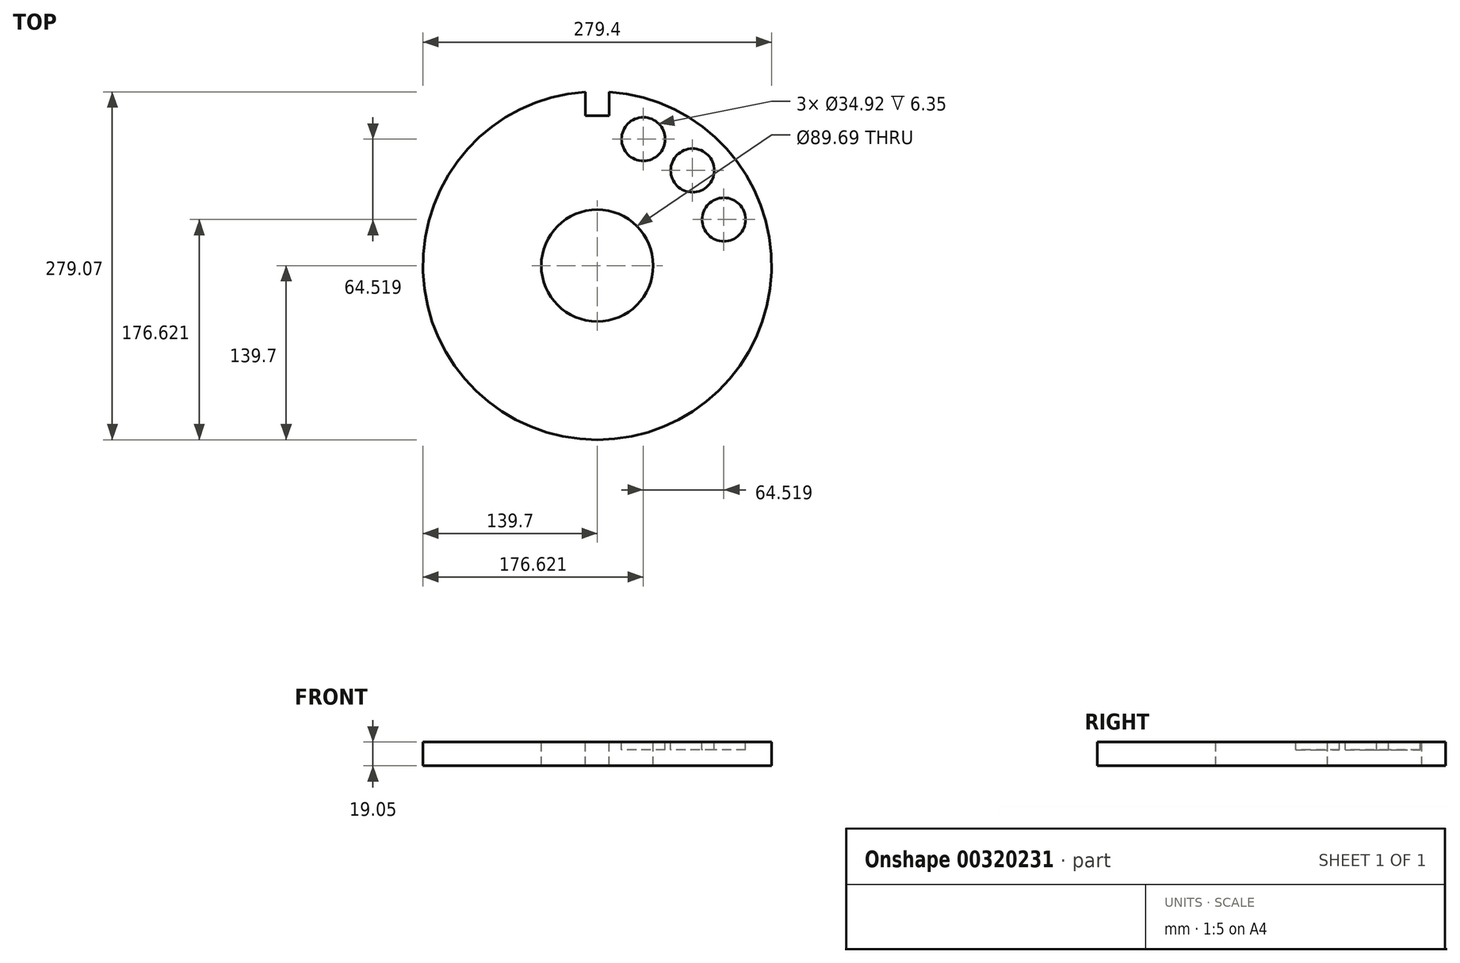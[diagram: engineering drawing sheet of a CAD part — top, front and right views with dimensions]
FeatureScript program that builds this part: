
annotation { "Feature Type Name" : "Feature", "Feature Type Description" : "" }
export const myFeature = defineFeature(function(context is Context, id is Id, definition is map)
    precondition{}
    {
        {
            var Q0;
            Q0=qCreatedBy(makeId("Top.planeOp"),FACE);
            var sketch = newSketch(context, id + "F0", { "sketchPlane" : qUnion([Q0])});
            skCircle(sketch, "E0", {"center": v(0, 0) * mm, "radius": 107.95 * mm, "construction": true});
            skCircle(sketch, "E1", {"center": v(0, 0) * mm, "radius": 139.7 * mm});
            skLineSegment(sketch, "E2", {"start": v(0, 0) * mm, "end": v(139.7, 0) * mm, "construction": true});
            skLineSegment(sketch, "E3", {"start": v(0, 0) * mm, "end": v(0, 139.7) * mm, "construction": true});
            skLineSegment(sketch, "E4", {"start": v(0, 0) * mm, "end": v(76.33, 76.33) * mm, "construction": true});
            skLineSegment(sketch, "E5", {"start": v(0, 0) * mm, "end": v(101.44, 36.92) * mm, "construction": true});
            skLineSegment(sketch, "E6", {"start": v(0, 0) * mm, "end": v(36.92, 101.44) * mm, "construction": true});
            skCircle(sketch, "E7", {"center": v(36.92, 101.44) * mm, "radius": 17.46 * mm});
            skCircle(sketch, "E8", {"center": v(76.33, 76.33) * mm, "radius": 17.46 * mm});
            skCircle(sketch, "E9", {"center": v(101.44, 36.92) * mm, "radius": 17.46 * mm});
            skLineSegment(sketch, "E10.top", {"start": v(-9.53, 113.97) * mm, "end": v(9.52, 113.97) * mm});
            skLineSegment(sketch, "E10.left", {"start": v(-9.53, 139.37) * mm, "end": v(-9.53, 113.97) * mm});
            skLineSegment(sketch, "E10.right", {"start": v(9.52, 139.37) * mm, "end": v(9.52, 113.97) * mm});
            skPoint(sketch, "E10.middle", {"position": v(0, 126.67) * mm});
            skLineSegment(sketch, "E11", {"start": v(-9.53, 120.32) * mm, "end": v(9.52, 120.32) * mm});
            skCircle(sketch, "E12", {"center": v(0, 0) * mm, "radius": 44.84 * mm});
            skSolve(sketch);
        }
        {
            var Q0;
            Q0=qSketchRegion(id+"F0",true);
            var Q1;
            Q1=makeQuery(id+"F0.imprint","IMPRINT",FACE,{"disambiguationData":[TD([[makeQuery(id+"F0.imprint","IMPRINT",EDGE,{"derivedFrom":sQuery(id+"F0.wireOp",EDGE,"E7")}),1.0]])]});
            var Q2;
            Q2=makeQuery(id+"F0.imprint","IMPRINT",FACE,{"disambiguationData":[TD([[makeQuery(id+"F0.imprint","IMPRINT",EDGE,{"derivedFrom":sQuery(id+"F0.wireOp",EDGE,"E8")}),1.0]])]});
            var Q3;
            Q3=makeQuery(id+"F0.imprint","IMPRINT",FACE,{"disambiguationData":[TD([[makeQuery(id+"F0.imprint","IMPRINT",EDGE,{"derivedFrom":sQuery(id+"F0.wireOp",EDGE,"E9")}),1.0]])]});
            var Q4;
            {var subQ0=sQuery(id+"F0.wireOp",EDGE,"E10.top");Q4=makeQuery(id+"F0.imprint","IMPRINT",FACE,{"disambiguationData":[TD([[makeQuery(id+"F0.imprint","IMPRINT",EDGE,{"derivedFrom":subQ0}),1.0]])]});}
            var Q5;
            Q5=makeQuery(id+"F0.imprint","IMPRINT",FACE,{"disambiguationData":[TD([[makeQuery(id+"F0.imprint","IMPRINT",EDGE,{"derivedFrom":sQuery(id+"F0.wireOp",EDGE,"E12")}),1.0]])]});
            extrude(context, id + "F1", {"entities" : qUnion([Q0, Q1, Q2, Q3, Q4, Q5]), "oppositeDirection" : true, "depth" : 19.05 * mm});
        }
        {
            var Q0;
            Q0=makeQuery(id+"F0.imprint","IMPRINT",FACE,{"disambiguationData":[TD([[makeQuery(id+"F0.imprint","IMPRINT",EDGE,{"derivedFrom":sQuery(id+"F0.wireOp",EDGE,"E7")}),1.0]])]});
            var Q1;
            Q1=makeQuery(id+"F0.imprint","IMPRINT",FACE,{"disambiguationData":[TD([[makeQuery(id+"F0.imprint","IMPRINT",EDGE,{"derivedFrom":sQuery(id+"F0.wireOp",EDGE,"E8")}),1.0]])]});
            var Q2;
            Q2=makeQuery(id+"F0.imprint","IMPRINT",FACE,{"disambiguationData":[TD([[makeQuery(id+"F0.imprint","IMPRINT",EDGE,{"derivedFrom":sQuery(id+"F0.wireOp",EDGE,"E9")}),1.0]])]});
            extrude(context, id + "F2", {"entities" : qUnion([Q0, Q1, Q2]), "operationType" : NewBodyOperationType.REMOVE, "oppositeDirection" : true, "depth" : 6.35 * mm});
        }
        {
            var Q0;
            {var subQ5=sQuery(id+"F0.wireOp",EDGE,"E11");Q0=makeQuery(id+"F0.imprint","IMPRINT",FACE,{"disambiguationData":[TD([[makeQuery(id+"F0.imprint","IMPRINT",EDGE,{"derivedFrom":subQ5}),1.0]])]});}
            extrude(context, id + "F3", {"entities" : qUnion([Q0]), "operationType" : NewBodyOperationType.REMOVE, "endBound" : BoundingType.THROUGH_ALL, "oppositeDirection" : true, "depth" : 25.4 * mm});
        }
        {
            var Q0;
            Q0=qCreatedBy(makeId("Front.planeOp"),FACE);
            var sketch = newSketch(context, id + "F4", { "sketchPlane" : qUnion([Q0])});
            skLineSegment(sketch, "E13", {"start": v(0, 0) * mm, "end": v(0, 89.72) * mm, "construction": true});
            skSolve(sketch);
        }
        {
            var Q0;
            Q0=makeQuery(id+"F0.imprint","IMPRINT",FACE,{"disambiguationData":[TD([[makeQuery(id+"F0.imprint","IMPRINT",EDGE,{"derivedFrom":sQuery(id+"F0.wireOp",EDGE,"E12")}),1.0]])]});
            extrude(context, id + "F5", {"entities" : qUnion([Q0]), "operationType" : NewBodyOperationType.REMOVE, "oppositeDirection" : true, "depth" : 25.4 * mm});
        }
    });
